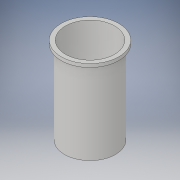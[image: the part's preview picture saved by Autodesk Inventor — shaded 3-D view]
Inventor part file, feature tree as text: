
AUTODESK INVENTOR PART (.ipt)
format: ipt  version: 2018 (Build 220112000, 112)  size: 112,128 bytes
history: native  units: in
note: dims shown in document units (in); Inventor stores cm internally (conversion verified against a paired STEP export)
features: extrude x3, sketch x3
ambient origin geometry x8: Origin, YZ Plane, XZ Plane, XY Plane, X Axis, Y Axis, Z Axis, Center Point
bodies: Solid1 (feature_tree)
feature tree (6):
  extrude  "Extrusion1"  Depth=14.5in
  extrude  "Extrusion2"  Depth=1.0in
  extrude  "Extrusion3"  Depth=0.5in TaperAngle=0.0deg
  sketch  "Sketch1"  dims[d0=17.0in d1=14.5in]
  sketch  "Sketch2"  dims[d2=1.0in d3=0.0in d4=15.0in]
  sketch  "Sketch3"  dims[d5=24.0in d6=0.0in d7=0.5in d8=0.0in]
